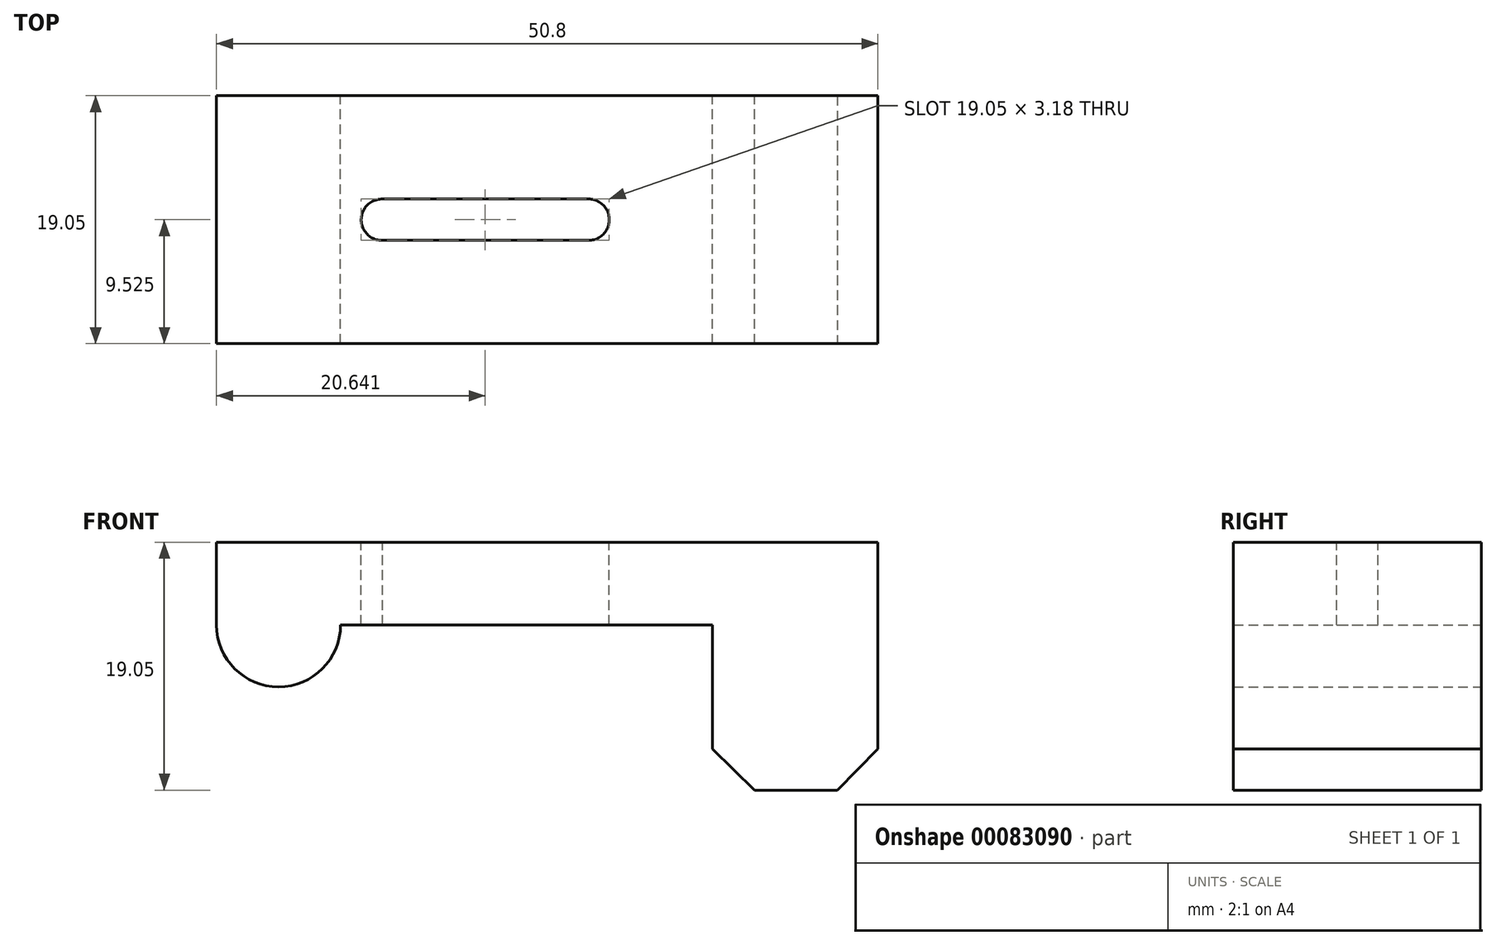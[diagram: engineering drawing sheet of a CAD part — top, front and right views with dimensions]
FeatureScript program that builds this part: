
annotation { "Feature Type Name" : "Feature", "Feature Type Description" : "" }
export const myFeature = defineFeature(function(context is Context, id is Id, definition is map)
    precondition{}
    {
        {
            var Q0;
            Q0=qCreatedBy(makeId("Front.planeOp"),FACE);
            var sketch = newSketch(context, id + "F0", { "sketchPlane" : qUnion([Q0])});
            skLineSegment(sketch, "E0", {"start": v(-31.8, 27.56) * mm, "end": v(19, 27.56) * mm});
            skLineSegment(sketch, "E1", {"start": v(19, 27.56) * mm, "end": v(19, 8.5) * mm});
            skLineSegment(sketch, "E2", {"start": v(19, 8.5) * mm, "end": v(6.3, 8.5) * mm});
            skLineSegment(sketch, "E3", {"start": v(6.3, 8.5) * mm, "end": v(6.3, 21.2) * mm});
            skLineSegment(sketch, "E4", {"start": v(6.3, 21.2) * mm, "end": v(-22.28, 21.2) * mm});
            skLineSegment(sketch, "E5", {"start": v(-31.8, 27.56) * mm, "end": v(-31.8, 21.2) * mm});
            skArc(sketch, "E6", {"start": v(-31.8, 21.2) * mm, "mid": v(-27.04, 16.45) * mm, "end": v(-22.28, 21.2) * mm});
            skSolve(sketch);
        }
        {
            var Q0;
            Q0=makeQuery(id+"F0.imprint","IMPRINT",FACE,{"disambiguationData":[TD([[makeQuery(id+"F0.imprint","IMPRINT",EDGE,{"derivedFrom":sQuery(id+"F0.wireOp",EDGE,"E0")}),-1.0]])]});
            extrude(context, id + "F1", {"entities" : qUnion([Q0]), "depth" : 19.05 * mm});
        }
        {
            var Q0;
            Q0=makeQuery(id+"F1.opExtrude","SWEPT_FACE",FACE,{"disambiguationData":[OSD([sQuery(id+"F0.wireOp",EDGE,"E0")])]});
            var sketch = newSketch(context, id + "F2", { "sketchPlane" : qUnion([Q0])});
            skArc(sketch, "E7", {"start": v(-19.06, -7.94) * mm, "mid": v(-20.7, -9.5) * mm, "end": v(-19.1, -11.11) * mm});
            skPoint(sketch, "E7.centerSnap0", {"position": v(-31.8, -9.53) * mm});
            skArc(sketch, "E8", {"start": v(-3.23, -11.11) * mm, "mid": v(-1.64, -9.52) * mm, "end": v(-3.23, -7.94) * mm});
            skLineSegment(sketch, "E9", {"start": v(-19.16, -7.94) * mm, "end": v(-3.23, -7.94) * mm});
            skLineSegment(sketch, "E10", {"start": v(-19.1, -11.11) * mm, "end": v(-3.23, -11.11) * mm});
            skSolve(sketch);
        }
        {
            var Q0;
            Q0 = qSketchRegion(id + "F2", true);
            extrude(context, id + "F3", {"entities" : qUnion([Q0]), "operationType" : NewBodyOperationType.REMOVE, "oppositeDirection" : true, "depth" : 31.18 * mm});
        }
        {
            var Q0;
            Q0=makeQuery(id+"F1.opExtrude","CAP_FACE",FACE,{"disambiguationData":[OSD([sQuery(id+"F0.wireOp",EDGE,"E0"),sQuery(id+"F0.wireOp",EDGE,"E1"),sQuery(id+"F0.wireOp",EDGE,"E2"),sQuery(id+"F0.wireOp",EDGE,"E3"),sQuery(id+"F0.wireOp",EDGE,"E4"),sQuery(id+"F0.wireOp",EDGE,"E5"),sQuery(id+"F0.wireOp",EDGE,"E6")])],"isStart":true});
            var sketch = newSketch(context, id + "F4", { "sketchPlane" : qUnion([Q0])});
            skLineSegment(sketch, "E11", {"start": v(-6.3, 11.68) * mm, "end": v(-9.53, 8.5) * mm});
            skLineSegment(sketch, "E12", {"start": v(-19, 11.68) * mm, "end": v(-16.07, 8.5) * mm});
            skSolve(sketch);
        }
        {
            var Q0;
            {var subQ0=sQuery(id+"F4.wireOp",EDGE,"E11");Q0=makeQuery(id+"F4.imprint","IMPRINT",FACE,{"disambiguationData":[TD([[makeQuery(id+"F4.imprint","IMPRINT",EDGE,{"derivedFrom":subQ0}),1.0]])]});}
            extrude(context, id + "F5", {"entities" : qUnion([Q0]), "operationType" : NewBodyOperationType.REMOVE, "oppositeDirection" : true, "depth" : 22.96 * mm});
        }
        {
            var Q0;
            Q0=makeQuery(id+"F1.opExtrude","CAP_FACE",FACE,{"disambiguationData":[OSD([sQuery(id+"F0.wireOp",EDGE,"E0"),sQuery(id+"F0.wireOp",EDGE,"E1"),sQuery(id+"F0.wireOp",EDGE,"E2"),sQuery(id+"F0.wireOp",EDGE,"E3"),sQuery(id+"F0.wireOp",EDGE,"E4"),sQuery(id+"F0.wireOp",EDGE,"E5"),sQuery(id+"F0.wireOp",EDGE,"E6")])],"isStart":false});
            var sketch = newSketch(context, id + "F6", { "sketchPlane" : qUnion([Q0])});
            skLineSegment(sketch, "E13", {"start": v(19, 11.68) * mm, "end": v(15.88, 8.5) * mm});
            skSolve(sketch);
        }
        {
            var Q0;
            {var subQ0=sQuery(id+"F6.wireOp",EDGE,"E13");Q0=makeQuery(id+"F6.imprint","IMPRINT",FACE,{"disambiguationData":[TD([[makeQuery(id+"F6.imprint","IMPRINT",EDGE,{"derivedFrom":subQ0}),1.0]])]});}
            extrude(context, id + "F7", {"entities" : qUnion([Q0]), "operationType" : NewBodyOperationType.REMOVE, "oppositeDirection" : true, "depth" : 30.07 * mm});
        }
    });
